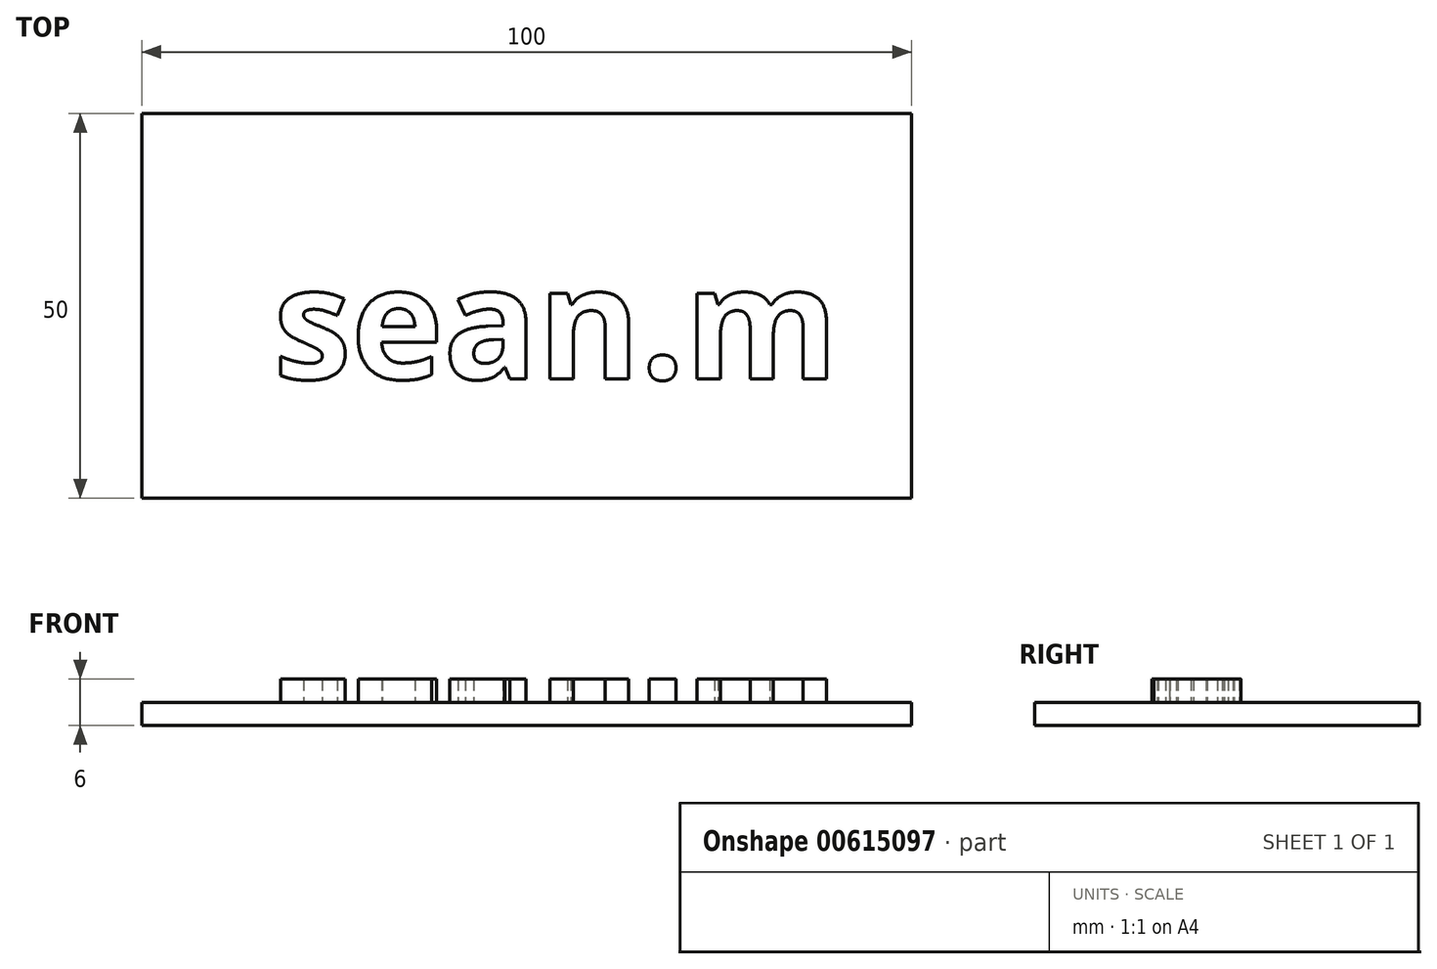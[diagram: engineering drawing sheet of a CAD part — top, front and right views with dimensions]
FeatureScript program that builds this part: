
annotation { "Feature Type Name" : "Feature", "Feature Type Description" : "" }
export const myFeature = defineFeature(function(context is Context, id is Id, definition is map)
    precondition{}
    {
        {
            var Q0;
            Q0=qCreatedBy(makeId("Top.planeOp"),FACE);
            var sketch = newSketch(context, id + "F0", { "sketchPlane" : qUnion([Q0])});
            skLineSegment(sketch, "E0.bottom", {"start": v(0, 0) * mm, "end": v(100, 0) * mm});
            skLineSegment(sketch, "E0.top", {"start": v(0, 50) * mm, "end": v(100, 50) * mm});
            skLineSegment(sketch, "E0.left", {"start": v(0, 0) * mm, "end": v(0, 50) * mm});
            skLineSegment(sketch, "E0.right", {"start": v(100, 0) * mm, "end": v(100, 50) * mm});
            skSolve(sketch);
        }
        {
            var Q0;
            Q0 = qSketchRegion(id + "F0", true);
            extrude(context, id + "F1", {"entities" : qUnion([Q0]), "depth" : 3 * mm, "offsetDistance" : 25 * mm});
        }
        {
            var Q0;
            Q0=makeQuery(id+"F1.opExtrude","CAP_FACE",FACE,{"disambiguationData":[OSD([sQuery(id+"F0.wireOp",EDGE,"E0.bottom"),sQuery(id+"F0.wireOp",EDGE,"E0.top"),sQuery(id+"F0.wireOp",EDGE,"E0.left"),sQuery(id+"F0.wireOp",EDGE,"E0.right")])],"isStart":false});
            var sketch = newSketch(context, id + "F2", { "sketchPlane" : qUnion([Q0])});
            skText(sketch, "E1", { "text": "sean.m\n", "fontName": "OpenSans-Bold.ttf"});
            const initialGuessF2  = {"E1": [0.0171, 0.01552, 1, 0, 0.01461]};
            skSetInitialGuess(sketch, initialGuessF2);
            skSolve(sketch);
        }
        {
            var Q0;
            Q0 = qSketchRegion(id + "F2", true);
            extrude(context, id + "F3", {"entities" : qUnion([Q0]), "operationType" : NewBodyOperationType.ADD, "depth" : 3 * mm, "offsetDistance" : 25 * mm});
        }
    });
